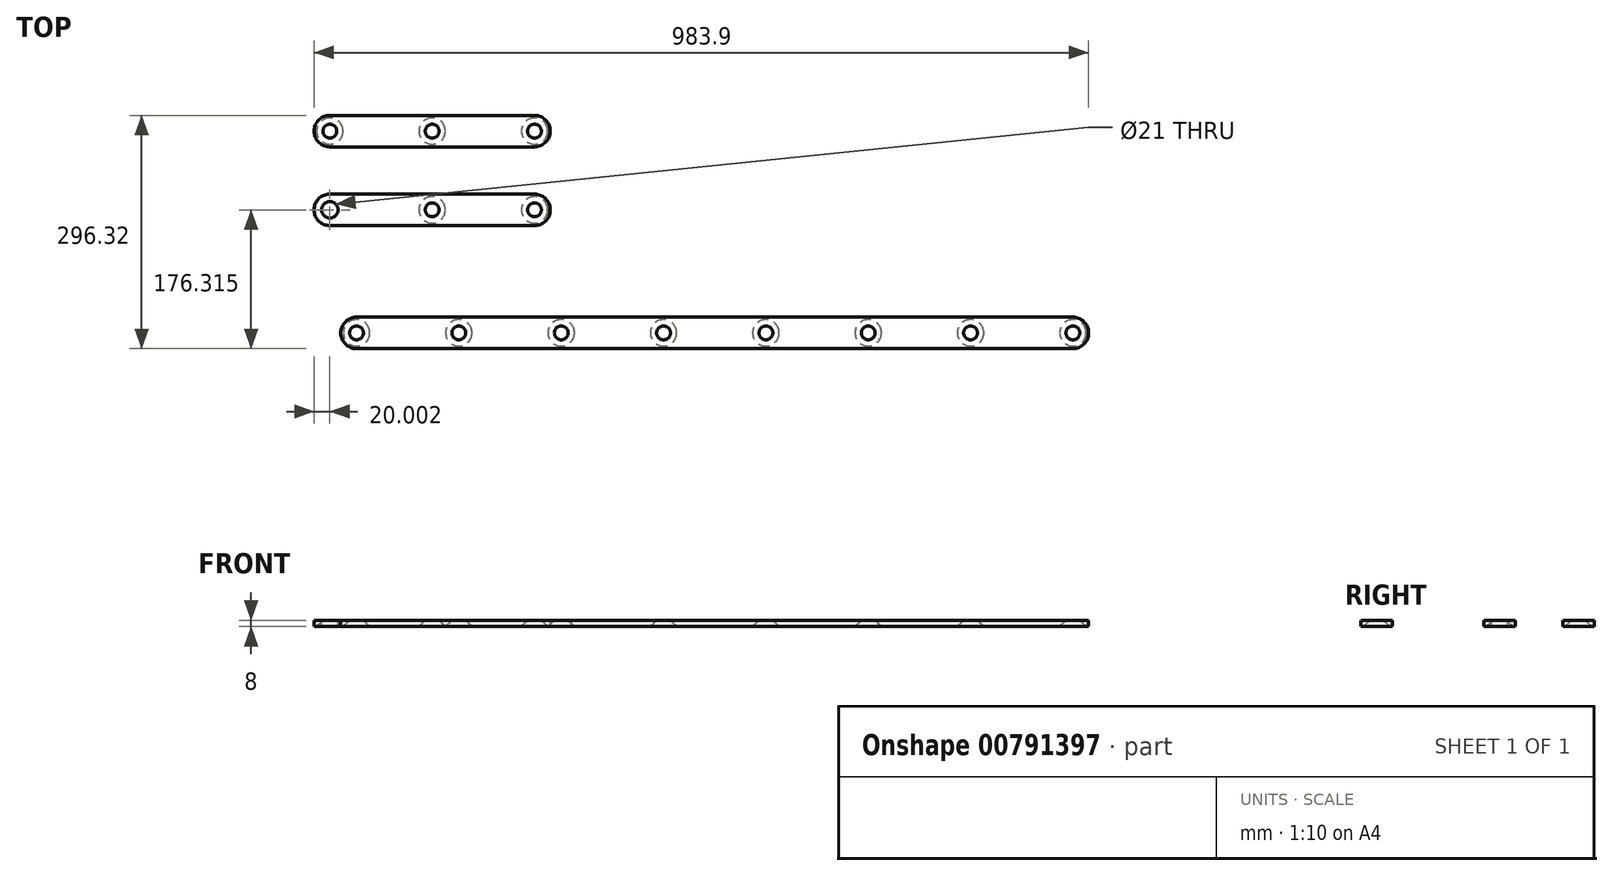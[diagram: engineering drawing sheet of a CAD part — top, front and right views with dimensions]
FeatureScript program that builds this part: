
annotation { "Feature Type Name" : "Feature", "Feature Type Description" : "" }
export const myFeature = defineFeature(function(context is Context, id is Id, definition is map)
    precondition{}
    {
        {
            var Q0;
            Q0=qCreatedBy(makeId("Top.planeOp"),FACE);
            var sketch = newSketch(context, id + "F0", { "sketchPlane" : qUnion([Q0])});
            skLineSegment(sketch, "E0.bottom", {"start": v(455, -20) * mm, "end": v(-455, -20) * mm});
            skLineSegment(sketch, "E0.top", {"start": v(455, 20) * mm, "end": v(-455, 20) * mm});
            skLineSegment(sketch, "E0.left", {"start": v(475, 0) * mm, "end": v(475, 0) * mm});
            skLineSegment(sketch, "E0.right", {"start": v(-475, 0) * mm, "end": v(-475, 0) * mm});
            skLineSegment(sketch, "E1", {"start": v(-475, -20) * mm, "end": v(475, 20) * mm, "construction": true});
            skPoint(sketch, "E2", {"position": v(-455, 0) * mm});
            skPoint(sketch, "E3.1.0.0", {"position": v(-325, 0) * mm});
            skPoint(sketch, "E3.2.0.0", {"position": v(-195, 0) * mm});
            skPoint(sketch, "E3.3.0.0", {"position": v(-65, 0) * mm});
            skPoint(sketch, "E3.4.0.0", {"position": v(65, 0) * mm});
            skPoint(sketch, "E3.5.0.0", {"position": v(195, 0) * mm});
            skPoint(sketch, "E3.6.0.0", {"position": v(325, 0) * mm});
            skPoint(sketch, "E3.7.0.0", {"position": v(455, 0) * mm});
            skLineSegment(sketch, "E3.direction1", {"start": v(-455, 0) * mm, "end": v(-325, 0) * mm, "construction": true});
            skLineSegment(sketch, "E4", {"start": v(-455, 0) * mm, "end": v(-475, -0.84) * mm, "construction": true});
            skLineSegment(sketch, "E5", {"start": v(455, 0) * mm, "end": v(475, 0) * mm, "construction": true});
            skPoint(sketch, "E6.visualSharp", {"position": v(-475, -20) * mm});
            skArc(sketch, "E6.filletArc", {"start": v(-475, 0) * mm, "mid": v(-469.14, -14.14) * mm, "end": v(-455, -20) * mm});
            skPoint(sketch, "E7.visualSharp", {"position": v(-475, 20) * mm});
            skArc(sketch, "E7.filletArc", {"start": v(-455, 20) * mm, "mid": v(-469.14, 14.14) * mm, "end": v(-475, 0) * mm});
            skPoint(sketch, "E8.visualSharp", {"position": v(475, 20) * mm});
            skArc(sketch, "E8.filletArc", {"start": v(475, 0) * mm, "mid": v(469.14, 14.14) * mm, "end": v(455, 20) * mm});
            skPoint(sketch, "E9.visualSharp", {"position": v(475, -20) * mm});
            skArc(sketch, "E9.filletArc", {"start": v(455, -20) * mm, "mid": v(469.14, -14.14) * mm, "end": v(475, 0) * mm});
            skSolve(sketch);
        }
        {
            var Q0;
            Q0 = qSketchRegion(id + "F0", true);
            extrude(context, id + "F1", {"entities" : qUnion([Q0]), "depth" : 8 * mm, "offsetDistance" : 25 * mm});
        }
        {
            var Q0;
            Q0=qCreatedBy(makeId("Top.planeOp"),FACE);
            var sketch = newSketch(context, id + "F2", { "sketchPlane" : qUnion([Q0])});
            skPoint(sketch, "E10", {"position": v(-455, 0) * mm});
            skPoint(sketch, "E11.1.0.0", {"position": v(-325, 0) * mm});
            skPoint(sketch, "E11.2.0.0", {"position": v(-195, 0) * mm});
            skPoint(sketch, "E11.3.0.0", {"position": v(-65, 0) * mm});
            skPoint(sketch, "E11.4.0.0", {"position": v(65, 0) * mm});
            skPoint(sketch, "E11.5.0.0", {"position": v(195, 0) * mm});
            skPoint(sketch, "E11.6.0.0", {"position": v(325, 0) * mm});
            skPoint(sketch, "E11.7.0.0", {"position": v(455, 0) * mm});
            skLineSegment(sketch, "E11.direction1", {"start": v(-455, 0) * mm, "end": v(-325, 0) * mm, "construction": true});
            skLineSegment(sketch, "E12", {"start": v(-455, 0) * mm, "end": v(-475, 0) * mm, "construction": true});
            skLineSegment(sketch, "E13", {"start": v(455, 0) * mm, "end": v(475, 0) * mm, "construction": true});
            skSolve(sketch);
        }
        {
            var Q0;
            Q0=sQuery(id+"F2.wireOp",VERTEX,"E10");
            var Q1;
            Q1=sQuery(id+"F2.wireOp",VERTEX,"E11.1.0.0");
            var Q2;
            Q2=sQuery(id+"F2.wireOp",VERTEX,"E11.2.0.0");
            var Q3;
            Q3=sQuery(id+"F2.wireOp",VERTEX,"E11.3.0.0");
            var Q4;
            Q4=sQuery(id+"F2.wireOp",VERTEX,"E11.4.0.0");
            var Q5;
            Q5=sQuery(id+"F2.wireOp",VERTEX,"E11.5.0.0");
            var Q6;
            Q6=sQuery(id+"F2.wireOp",VERTEX,"E11.6.0.0");
            var Q7;
            Q7=sQuery(id+"F2.wireOp",VERTEX,"E11.7.0.0");
            var Q8;
            Q8=makeQuery(id+"F1.opExtrude","SWEPT_BODY",BODY,{"disambiguationData":[OSD([sQuery(id+"F0.wireOp",EDGE,"E0.bottom"),sQuery(id+"F0.wireOp",EDGE,"E0.top"),sQuery(id+"F0.wireOp",EDGE,"E0.left"),sQuery(id+"F0.wireOp",EDGE,"E0.right")])]});
            hole(context, id + "F3", {"style" : HoleStyle.C_SINK, "endStyle" : HoleEndStyle.THROUGH, "oppositeDirection" : true, "standardTappedOrClearance" : lookupTablePath({ "fit" : "Normal", "standard" : "ISO", "size" : "M16", "type" : "Clearance" }), "standardBlindInLast" : lookupTablePath({ "fit" : "Normal", "standard" : "ISO", "engagement" : "75%", "pitch" : "2 mm", "size" : "M16", "type" : "Clearance & tapped" }), "holeDiameter" : 17.5 * mm, "cSinkDiameter" : 33.6 * mm, "cSinkAngle" : 90 * degree, "majorDiameter" : 16 * mm, "isTappedThrough" : true, "tappedDepth" : 12 * mm, "tapClearance" : 3, "locations" : qUnion([Q0, Q1, Q2, Q3, Q4, Q5, Q6, Q7]), "scope" : qUnion([Q8]), "startStyle" : HoleStartStyle.SKETCH});
        }
        {
            var Q0;
            Q0=qCreatedBy(makeId("Top.planeOp"),FACE);
            var sketch = newSketch(context, id + "F4", { "sketchPlane" : qUnion([Q0])});
            skLineSegment(sketch, "E14.bottom", {"start": v(-228.9, 136.32) * mm, "end": v(-488.9, 136.32) * mm});
            skLineSegment(sketch, "E14.top", {"start": v(-228.9, 176.32) * mm, "end": v(-488.9, 176.32) * mm});
            skLineSegment(sketch, "E14.left", {"start": v(-208.9, 156.32) * mm, "end": v(-208.9, 156.32) * mm});
            skLineSegment(sketch, "E14.right", {"start": v(-508.9, 156.32) * mm, "end": v(-508.9, 156.32) * mm});
            skPoint(sketch, "E15.visualSharp", {"position": v(-508.9, 136.32) * mm});
            skArc(sketch, "E15.filletArc", {"start": v(-508.9, 156.32) * mm, "mid": v(-503.04, 142.17) * mm, "end": v(-488.9, 136.32) * mm});
            skPoint(sketch, "E16.visualSharp", {"position": v(-508.9, 176.32) * mm});
            skArc(sketch, "E16.filletArc", {"start": v(-488.9, 176.32) * mm, "mid": v(-503.04, 170.46) * mm, "end": v(-508.9, 156.32) * mm});
            skPoint(sketch, "E17.visualSharp", {"position": v(-208.9, 176.32) * mm});
            skArc(sketch, "E17.filletArc", {"start": v(-208.9, 156.32) * mm, "mid": v(-214.76, 170.46) * mm, "end": v(-228.9, 176.32) * mm});
            skPoint(sketch, "E18.visualSharp", {"position": v(-208.9, 136.32) * mm});
            skArc(sketch, "E18.filletArc", {"start": v(-228.9, 136.32) * mm, "mid": v(-214.76, 142.17) * mm, "end": v(-208.9, 156.32) * mm});
            skSolve(sketch);
        }
        {
            var Q0;
            Q0 = qSketchRegion(id + "F4", true);
            extrude(context, id + "F5", {"entities" : qUnion([Q0]), "depth" : 8 * mm, "offsetDistance" : 25 * mm});
        }
        {
            var Q0;
            Q0=makeQuery(id+"F5.opExtrude","CAP_FACE",FACE,{"disambiguationData":[OSD([sQuery(id+"F4.wireOp",EDGE,"E14.bottom"),sQuery(id+"F4.wireOp",EDGE,"E14.top"),sQuery(id+"F4.wireOp",EDGE,"E14.left"),sQuery(id+"F4.wireOp",EDGE,"E14.right")])],"isStart":true});
            var sketch = newSketch(context, id + "F6", { "sketchPlane" : qUnion([Q0])});
            skPoint(sketch, "E19", {"position": v(-488.9, -156.32) * mm});
            skLineSegment(sketch, "E20", {"start": v(-108.9, -156.32) * mm, "end": v(-358.9, -156.32) * mm, "construction": true});
            skPoint(sketch, "E21", {"position": v(-358.9, -156.32) * mm});
            skPoint(sketch, "E22", {"position": v(-228.9, -156.32) * mm});
            skSolve(sketch);
        }
        {
            var Q0;
            Q0=sQuery(id+"F6.wireOp",VERTEX,"E21");
            var Q1;
            Q1=sQuery(id+"F6.wireOp",VERTEX,"E22");
            var Q2;
            Q2=makeQuery(id+"F5.opExtrude","SWEPT_BODY",BODY,{"disambiguationData":[OSD([sQuery(id+"F4.wireOp",EDGE,"E14.bottom"),sQuery(id+"F4.wireOp",EDGE,"E14.top"),sQuery(id+"F4.wireOp",EDGE,"E14.left"),sQuery(id+"F4.wireOp",EDGE,"E14.right")])]});
            hole(context, id + "F7", {"style" : HoleStyle.C_SINK, "endStyle" : HoleEndStyle.THROUGH, "standardTappedOrClearance" : lookupTablePath({ "fit" : "Normal", "standard" : "ISO", "size" : "M16", "type" : "Clearance" }), "standardBlindInLast" : lookupTablePath({ "fit" : "Normal", "standard" : "ISO", "engagement" : "75%", "pitch" : "2 mm", "size" : "M16", "type" : "Clearance & tapped" }), "holeDiameter" : 17.5 * mm, "cSinkDiameter" : 33.6 * mm, "cSinkAngle" : 90 * degree, "majorDiameter" : 5 * mm, "isTappedThrough" : true, "tappedDepth" : 12 * mm, "tapClearance" : 3, "locations" : qUnion([Q0, Q1]), "scope" : qUnion([Q2]), "startStyle" : HoleStartStyle.SKETCH});
        }
        {
            var Q0;
            Q0=makeQuery(id+"F5.opExtrude","SWEPT_BODY",BODY,{"disambiguationData":[OSD([sQuery(id+"F4.wireOp",EDGE,"E14.bottom"),sQuery(id+"F4.wireOp",EDGE,"E14.top"),sQuery(id+"F4.wireOp",EDGE,"E15.filletArc"),sQuery(id+"F4.wireOp",EDGE,"E16.filletArc"),sQuery(id+"F4.wireOp",EDGE,"E17.filletArc"),sQuery(id+"F4.wireOp",EDGE,"E18.filletArc")])]});
            transform(context, id + "F8", {"entities" : qUnion([Q0]), "transformType" : TransformType.TRANSLATION_3D, "dx" : 0 * mm, "dy" : 100 * mm, "dz" : 0 * mm, "makeCopy" : true});
        }
        {
            var Q0;
            Q0=sQuery(id+"F6.wireOp",VERTEX,"E19");
            var Q1;
            Q1=makeQuery(id+"F5.opExtrude","SWEPT_BODY",BODY,{"disambiguationData":[OSD([sQuery(id+"F4.wireOp",EDGE,"E14.bottom"),sQuery(id+"F4.wireOp",EDGE,"E14.top"),sQuery(id+"F4.wireOp",EDGE,"E15.filletArc"),sQuery(id+"F4.wireOp",EDGE,"E16.filletArc"),sQuery(id+"F4.wireOp",EDGE,"E17.filletArc"),sQuery(id+"F4.wireOp",EDGE,"E18.filletArc")])]});
            hole(context, id + "F9", {"style" : HoleStyle.SIMPLE, "endStyle" : HoleEndStyle.THROUGH, "standardTappedOrClearance" : lookupTablePath({ "fit" : "Loose", "standard" : "ISO", "size" : "M18", "type" : "Clearance" }), "standardBlindInLast" : lookupTablePath({ "fit" : "Loose", "standard" : "ISO", "engagement" : "75%", "pitch" : "1.5 mm", "size" : "M18", "type" : "Clearance & tapped" }), "holeDiameter" : 21 * mm, "majorDiameter" : 5 * mm, "isTappedThrough" : true, "tappedDepth" : 12 * mm, "tapClearance" : 3, "locations" : qUnion([Q0]), "scope" : qUnion([Q1]), "startStyle" : HoleStartStyle.SKETCH});
        }
        {
            var Q0;
            Q0=makeQuery(id+"F8.opPattern","COPY",FACE,{"derivedFrom":makeQuery(id+"F5.opExtrude","CAP_FACE",FACE,{"disambiguationData":[OSD([sQuery(id+"F4.wireOp",EDGE,"E14.bottom"),sQuery(id+"F4.wireOp",EDGE,"E14.top"),sQuery(id+"F4.wireOp",EDGE,"E15.filletArc"),sQuery(id+"F4.wireOp",EDGE,"E16.filletArc"),sQuery(id+"F4.wireOp",EDGE,"E17.filletArc"),sQuery(id+"F4.wireOp",EDGE,"E18.filletArc")])],"isStart":true}),"instanceName":"1"});
            var sketch = newSketch(context, id + "F10", { "sketchPlane" : qUnion([Q0])});
            skPoint(sketch, "E23", {"position": v(-488.9, -256.32) * mm});
            skSolve(sketch);
        }
        {
            var Q0;
            Q0=sQuery(id+"F10.wireOp",VERTEX,"E23");
            var Q1;
            Q1=makeQuery(id+"F8.opPattern","COPY",BODY,{"derivedFrom":makeQuery(id+"F5.opExtrude","SWEPT_BODY",BODY,{"disambiguationData":[OSD([sQuery(id+"F4.wireOp",EDGE,"E14.bottom"),sQuery(id+"F4.wireOp",EDGE,"E14.top"),sQuery(id+"F4.wireOp",EDGE,"E15.filletArc"),sQuery(id+"F4.wireOp",EDGE,"E16.filletArc"),sQuery(id+"F4.wireOp",EDGE,"E17.filletArc"),sQuery(id+"F4.wireOp",EDGE,"E18.filletArc")])]}),"instanceName":"1"});
            hole(context, id + "F11", {"style" : HoleStyle.C_SINK, "endStyle" : HoleEndStyle.THROUGH, "standardTappedOrClearance" : lookupTablePath({ "fit" : "Normal", "standard" : "ISO", "size" : "M16", "type" : "Clearance" }), "standardBlindInLast" : lookupTablePath({ "fit" : "Normal", "standard" : "ISO", "engagement" : "75%", "pitch" : "2 mm", "size" : "M16", "type" : "Clearance & tapped" }), "holeDiameter" : 17.5 * mm, "cSinkDiameter" : 33.6 * mm, "cSinkAngle" : 90 * degree, "majorDiameter" : 5 * mm, "isTappedThrough" : true, "tappedDepth" : 12 * mm, "tapClearance" : 3, "locations" : qUnion([Q0]), "scope" : qUnion([Q1]), "startStyle" : HoleStartStyle.SKETCH});
        }
    });
